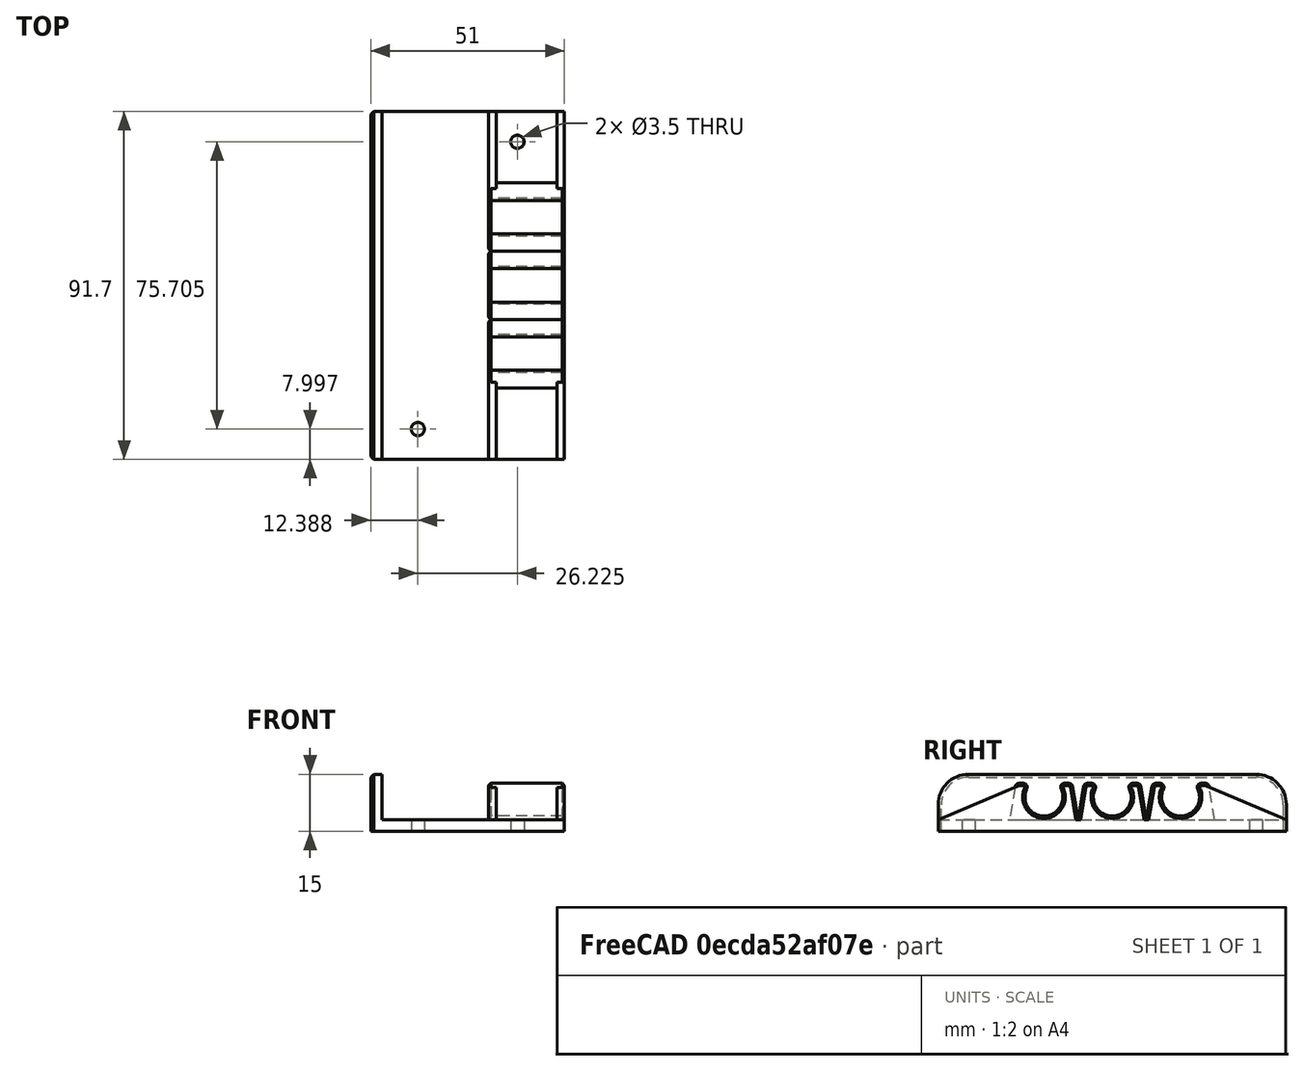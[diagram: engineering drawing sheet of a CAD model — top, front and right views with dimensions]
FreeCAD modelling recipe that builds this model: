
FCSTD DOCUMENT  (FreeCAD 0.21R33771 (Git))
Label: SDS-Plus_ClipHolder
License: All rights reserved
LicenseURL: https://en.wikipedia.org/wiki/All_rights_reserved
objects: Sketcher::SketchObject×7, PartDesign::Pad×6, PartDesign::Chamfer×4, PartDesign::LinearPattern×2, PartDesign::Body×2, PartDesign::SubShapeBinder×2, PartDesign::Fillet×1, PartDesign::FeatureBase×1, Mesh::Feature×1, Part::Feature×1, Spreadsheet::Sheet×1, PartDesign::Hole×1
note: 39 computed .brp shape members not serialized (recipe doc carries the construction recipe); baked Part::Feature solids carry a one-line shape summary decoded from their .brp

FEATURE [Sketcher::SketchObject] Sketch
  FullyConstrained = true
  MapMode = 5
  Placement = pos=(0,0,0) rot=(0.57735,0.57735,0.57735;2.0944rad)
  Support = -> [YZ_Plane]
  sketch-geometry (15):
    g0: ArcOfCircle CenterX=9 CenterY=6 CenterZ=0 NormalX=0 NormalY=0 NormalZ=1 AngleXU=0 Radius=5 StartAngle=2.69057 EndAngle=6.73421
    g1: LineSegment StartX=3.6 StartY=9.61534 StartZ=0 EndX=2.44735 EndY=9.61534 EndZ=0
    g2: LineSegment StartX=1.46091 StartY=8.77948 StartZ=0 EndX=0 EndY=0 EndZ=0
    g3: LineSegment StartX=0 StartY=0 StartZ=0 EndX=18 EndY=0 EndZ=0
    g4: LineSegment StartX=18 StartY=0 StartZ=0 EndX=16.5391 EndY=8.77948 EndZ=0
    g5: LineSegment StartX=15.5527 StartY=9.61534 StartZ=0 EndX=14.4 EndY=9.61534 EndZ=0
    g6: LineSegment StartX=9 StartY=6 StartZ=0 EndX=9 EndY=1 EndZ=0
    g7: LineSegment StartX=9 StartY=6 StartZ=0 EndX=4 EndY=6 EndZ=0
    g8: ArcOfCircle CenterX=3.6 CenterY=8.61534 CenterZ=0 NormalX=0 NormalY=0 NormalZ=1 AngleXU=0 Radius=1 StartAngle=5.83216 EndAngle=7.85398
    g9: ArcOfCircle CenterX=14.4 CenterY=8.61534 CenterZ=0 NormalX=0 NormalY=0 NormalZ=1 AngleXU=0 Radius=1 StartAngle=1.5708 EndAngle=3.59262
    g10: LineSegment StartX=4.5 StartY=8.17945 StartZ=0 EndX=13.5 EndY=8.17945 EndZ=0
    g11: ArcOfCircle CenterX=15.5527 CenterY=8.61534 CenterZ=0 NormalX=0 NormalY=0 NormalZ=1 AngleXU=0 Radius=1 StartAngle=0.16489 EndAngle=1.5708
    g12: GeomPoint X=16.4 Y=9.61534 Z=0
    g13: ArcOfCircle CenterX=2.44735 CenterY=8.61534 CenterZ=0 NormalX=0 NormalY=0 NormalZ=1 AngleXU=0 Radius=1 StartAngle=1.5708 EndAngle=2.9767
    g14: GeomPoint X=1.6 Y=9.61534 Z=0
  constraints (38):
    c: Diameter(g0) = 10
    c: Horizontal(g1)
    c: Coincident(g2,g-1)
    c: Coincident(g2,g3)
    c: PointOnObject(g3,g-1)
    c: Coincident(g3,g4)
    c: Horizontal(g5)
    c: Coincident(g6,g0)
    c: PointOnObject(g6,g0)
    c: Vertical(g6)
    c: Coincident(g7,g0)
    c: PointOnObject(g7,g0)
    c: Horizontal(g7)
    c: DistanceY(g2,g6) = 1
    c: DistanceX(g2,g7) = 4
    c: Tangent(g1,g8) = -1.5708
    c: Tangent(g0,g8) = 1.5708
    c: Tangent(g0,g9) = 1.5708
    c: Tangent(g5,g9) = -1.5708
    c: Equal(g8,g9)
    c: Coincident(g10,g0)
    c: Coincident(g10,g0)
    c: Horizontal(g10)
    c: DistanceX(g10,g10) = 9
    c: Radius(g8) = 1
    c: DistanceX(g3,g3) = 18
    c: DistanceX(g5,g12) = 2
    c: PointOnObject(g12,g5)
    c: PointOnObject(g12,g4)
    c: Tangent(g5,g11) = -1.5708
    c: Tangent(g4,g11) = -1.5708
    c: PointOnObject(g14,g1)
    c: PointOnObject(g14,g2)
    c: Tangent(g1,g13) = -1.5708
    c: Tangent(g2,g13) = -1.5708
    c: Equal(g11,g13)
    c: Radius(g13) = 1
    c: DistanceX(g14,g1) = 2
FEATURE [PartDesign::Pad] Pad
  Direction = (1,-2e-16,3e-16)
  Length = 20
  Length2 = 10
  Placement = pos=(0,0,0) rot=(1,1,1;2.0944rad)
  Profile = -> Sketch
  ReferenceAxis = -> Sketch [N_Axis]
  Type = 0
FEATURE [Sketcher::SketchObject] Sketch001
  FullyConstrained = true
  MapMode = 5
  Placement = pos=(0,0,0) rot=(1,0,0;1.5708rad)
  Support = -> [XZ_Plane]
  sketch-geometry (6):
    g0: LineSegment StartX=20 StartY=-3 StartZ=0 EndX=-31 EndY=-3 EndZ=0
    g1: LineSegment StartX=-28 StartY=0 StartZ=0 EndX=20 EndY=0 EndZ=0
    g2: LineSegment StartX=20 StartY=0 StartZ=0 EndX=20 EndY=-3 EndZ=0
    g3: LineSegment StartX=-31 StartY=-3 StartZ=0 EndX=-31 EndY=11 EndZ=0
    g4: LineSegment StartX=-31 StartY=11 StartZ=0 EndX=-28 EndY=11 EndZ=0
    g5: LineSegment StartX=-28 StartY=11 StartZ=0 EndX=-28 EndY=0 EndZ=0
  constraints (18):
    c: Coincident(g1,g2)
    c: Coincident(g2,g0)
    c: Horizontal(g0)
    c: Horizontal(g1)
    c: Vertical(g2)
    c: PointOnObject(g1,g-1)
    c: DistanceX(g-1,g1) = 20
    c: DistanceX(g1,g-1) = 28
    c: Coincident(g0,g3)
    c: Vertical(g3)
    c: Coincident(g3,g4)
    c: Horizontal(g4)
    c: Coincident(g4,g5)
    c: Coincident(g5,g1)
    c: Vertical(g5)
    c: DistanceX(g4,g4) = 3
    c: DistanceY(g2,g2) = 3
    c: DistanceY(g5,g5) = 11
FEATURE [PartDesign::Chamfer] Chamfer
  Angle = 45
  Base = -> Pad [Edge25,Edge28,Edge30,Edge4,Edge7,Edge10,Edge13,Edge16,Edge19,Edge18,Edge15,Edge12,Edge9,Edge6,Edge3,Edge29,Edge27,Edge24]
  BaseFeature = -> Pad
  ChamferType = 0
  FlipDirection = false
  Placement = pos=(0,0,0) rot=(1,1,1;2.0944rad)
  Size = 0.6
  Size2 = 1
  SupportTransform = false
  UseAllEdges = false
FEATURE [PartDesign::Pad] Pad001
  BaseFeature = -> Chamfer
  Direction = (0,-1,-2e-16)
  Length = 18
  Length2 = 10
  Placement = pos=(0,0,0) rot=(1,1,1;2.0944rad)
  Profile = -> Sketch001
  ReferenceAxis = -> Sketch001 [N_Axis]
  Reversed = true
  Type = 0
FEATURE [PartDesign::LinearPattern] LinearPattern
  BaseFeature = -> Pad001
  Direction = -> Sketch001 [N_Axis]
  Length = 36
  Occurrences = 3
  Originals = -> [Pad001,Pad,Chamfer]
  Placement = pos=(0,0,0) rot=(1,1,1;2.0944rad)
FEATURE [PartDesign::Fillet] Fillet
  Base = -> LinearPattern [Edge118,Edge148]
  BaseFeature = -> LinearPattern
  Placement = pos=(0,0,0) rot=(1,1,1;2.0944rad)
  Radius = 8
  SupportTransform = false
  UseAllEdges = false
FEATURE [PartDesign::Chamfer] Chamfer001
  Angle = 45
  Base = -> Fillet [Edge5,Edge118]
  BaseFeature = -> Fillet
  ChamferType = 0
  FlipDirection = false
  Placement = pos=(0,0,0) rot=(1,1,1;2.0944rad)
  Size = 0.6
  Size2 = 1
  SupportTransform = false
  UseAllEdges = false
FEATURE [PartDesign::Chamfer] Chamfer002
  Angle = 45
  Base = -> Chamfer001 [Edge3,Edge16,Edge15,Edge40,Edge85,Edge86,Edge94,Edge93,Edge49,Edge25,Edge22,Vertex6,Edge95,Edge7,Edge87,Edge124,Edge8]
  BaseFeature = -> Chamfer001
  ChamferType = 0
  FlipDirection = false
  Placement = pos=(0,0,0) rot=(1,1,1;2.0944rad)
  Size = 0.6
  Size2 = 1
  SupportTransform = false
  UseAllEdges = false
FEATURE [PartDesign::Body] Body  label="SDS Clip Body"
  Group = -> [Sketch,Pad,Sketch001,Chamfer,Pad001,LinearPattern,Fillet,Chamfer001,Chamfer002]
  Origin = -> Origin
  Tip = -> Chamfer002
FEATURE [PartDesign::FeatureBase] BaseFeature
  BaseFeature = -> Body
FEATURE [Mesh::Feature] L_Boxx_Lid_Mount_Body  label="L-Boxx_Lid_Mount-Body"
FEATURE [Part::Feature] L_Boxx_Lid_Mount_Body001
  shape: bbox 38.95 x 88.43 x 1 mm, 228 faces, 0 solids (baked)
FEATURE [PartDesign::SubShapeBinder] Binder  label="L-Boxx-lid-mount"
  BindCopyOnChange = 0
  BindMode = 0
  ClaimChildren = false
  Context = -> Body001 [Binder.]
  Fuse = false
  MakeFace = true
  OffsetFill = false
  OffsetIntersection = false
  OffsetJoinType = 0
  OffsetOpenResult = false
  PartialLoad = false
  Relative = true
  Support = -> [L_Boxx_Lid_Mount_Body001]
  _Version = 2
FEATURE [Sketcher::SketchObject] Sketch002  label="OriginalMountHoleSketch"
  ExternalGeometry = -> [Binder,BaseFeature]
  FullyConstrained = true
  MapMode = 5
  Support = -> [XY_Plane001]
  sketch-geometry (2):
    g0: Circle CenterX=26.2251 CenterY=45.4231 CenterZ=0 NormalX=0 NormalY=0 NormalZ=1 AngleXU=0 Radius=1.50002
    g1: Circle CenterX=0.000238433 CenterY=-30.282 CenterZ=0 NormalX=0 NormalY=0 NormalZ=1 AngleXU=0 Radius=1.50002
  constraints (10):
    c: PointOnObject(g-5,g0)
    c: PointOnObject(g-5,g0)
    c: PointOnObject(g-7,g0)
    c: PointOnObject(g-3,g1)
    c: PointOnObject(g-3,g1)
    c: PointOnObject(g-4,g1)
    c: DistanceY(g-9,g0) = 27.4231  'y1'
    c: DistanceY(g-8,g1) = 5.71795  'y2'
    c: DistanceX(g-9,g0) = 6.82513  'x1'
    c: DistanceX(g-8,g1) = 30.4002  'x2'
FEATURE [PartDesign::SubShapeBinder] Binder001
  BindCopyOnChange = 0
  BindMode = 0
  ClaimChildren = false
  Context = -> Body001 [Binder001.]
  Fuse = false
  MakeFace = true
  OffsetFill = false
  OffsetIntersection = false
  OffsetJoinType = 0
  OffsetOpenResult = false
  PartialLoad = false
  Placement = pos=(-18.6127,-16.5705,0) rot=(0,0,1;0rad)
  Relative = true
  Support = -> [Sketch002]
  _Version = 2
  expr: .Placement.Base.x = <<offset>>.x
  expr: .Placement.Base.y = <<offset>>.y
FEATURE [Spreadsheet::Sheet] Spreadsheet  label="offset"
  cells = A1='x; B1(x)==-(x2 + x1) / 2; A2='y; B2(y)==-(y1 + y2) / 2; A4='x1; B4(x1)==<<OriginalMountHoleSketch>>.Constraints.x1; A5='x2; B5(x2)==<<OriginalMountHoleSketch>>.Constraints.x2; A6='y1; B6(y1)==<<OriginalMountHoleSketch>>.Constraints.y1; A7='y2; B7(y2)==<<OriginalMountHoleSketch>>.Constraints.y2
FEATURE [Sketcher::SketchObject] Sketch003
  ExternalGeometry = -> [BaseFeature,Binder001]
  FullyConstrained = true
  MapMode = 5
  Support = -> [XY_Plane001]
  sketch-geometry (6):
    g0: LineSegment StartX=-31 StartY=-54.8526 StartZ=0 EndX=20 EndY=-54.8526 EndZ=0
    g1: LineSegment StartX=20 StartY=-54.8526 StartZ=0 EndX=20 EndY=36.8526 EndZ=0
    g2: LineSegment StartX=20 StartY=36.8526 StartZ=0 EndX=-31 EndY=36.8526 EndZ=0
    g3: LineSegment StartX=-31 StartY=36.8526 StartZ=0 EndX=-31 EndY=-54.8526 EndZ=0
    g4: LineSegment StartX=-18.6124 StartY=-46.8526 StartZ=0 EndX=-18.6124 EndY=-54.8526 EndZ=0
    g5: LineSegment StartX=7.61245 StartY=28.8526 StartZ=0 EndX=7.61245 EndY=36.8526 EndZ=0
  constraints (18):
    c: Coincident(g0,g1)
    c: Coincident(g1,g2)
    c: Coincident(g2,g3)
    c: Coincident(g3,g0)
    c: Horizontal(g0)
    c: Horizontal(g2)
    c: Vertical(g1)
    c: Vertical(g3)
    c: PointOnObject(g-3,g3)
    c: PointOnObject(g-4,g1)
    c: Coincident(g4,g-6)
    c: PointOnObject(g4,g0)
    c: Vertical(g4)
    c: Coincident(g5,g-5)
    c: PointOnObject(g5,g2)
    c: Vertical(g5)
    c: Equal(g5,g4)
    c: DistanceY(g4,g4) = 8
FEATURE [PartDesign::Pad] Pad002
  BaseFeature = -> BaseFeature
  Direction = (0,0,1)
  Length = 3
  Length2 = 10
  Profile = -> Sketch003
  ReferenceAxis = -> Sketch003 [N_Axis]
  Reversed = true
  Type = 0
FEATURE [Sketcher::SketchObject] Sketch004
  ExternalGeometry = -> [Pad002]
  FullyConstrained = true
  MapMode = 5
  Placement = pos=(0,0,0) rot=(0.57735,0.57735,0.57735;2.0944rad)
  Support = -> [YZ_Plane001]
  sketch-geometry (3):
    g0: LineSegment StartX=-54.8526 StartY=0 StartZ=0 EndX=-33.5527 EndY=0 EndZ=0
    g1: LineSegment StartX=-33.5527 StartY=0 StartZ=0 EndX=-33.5527 EndY=9.01534 EndZ=0
    g2: LineSegment StartX=-33.5527 StartY=9.01534 StartZ=0 EndX=-54.8526 EndY=0 EndZ=0
  constraints (7):
    c: Coincident(g-4,g0)
    c: Horizontal(g0)
    c: Coincident(g0,g1)
    c: Coincident(g1,g2)
    c: Coincident(g2,g0)
    c: Coincident(g1,g-3)
    c: Vertical(g1)
FEATURE [PartDesign::Pad] Pad003
  BaseFeature = -> Pad002
  Direction = (1,-2e-16,3e-16)
  Length = 2
  Length2 = 10
  Profile = -> Sketch004
  ReferenceAxis = -> Sketch004 [N_Axis]
  Type = 0
FEATURE [Sketcher::SketchObject] Sketch005
  ExternalGeometry = -> [Pad003]
  FullyConstrained = true
  MapMode = 5
  Placement = pos=(0,0,0) rot=(0.57735,0.57735,0.57735;2.0944rad)
  Support = -> [YZ_Plane001]
  sketch-geometry (3):
    g0: LineSegment StartX=15.5527 StartY=9.01534 StartZ=0 EndX=15.5527 EndY=0 EndZ=0
    g1: LineSegment StartX=15.5527 StartY=0 StartZ=0 EndX=36.8526 EndY=0 EndZ=0
    g2: LineSegment StartX=36.8526 StartY=0 StartZ=0 EndX=15.5527 EndY=9.01534 EndZ=0
  constraints (7):
    c: Coincident(g-4,g0)
    c: PointOnObject(g0,g-1)
    c: Vertical(g0)
    c: Coincident(g0,g1)
    c: Coincident(g1,g-3)
    c: Coincident(g1,g2)
    c: Coincident(g2,g0)
FEATURE [PartDesign::Pad] Pad004
  BaseFeature = -> Pad003
  Direction = (1,-2e-16,3e-16)
  Length = 2
  Length2 = 10
  Profile = -> Sketch005
  ReferenceAxis = -> Sketch005 [N_Axis]
  Type = 0
FEATURE [PartDesign::LinearPattern] LinearPattern001
  BaseFeature = -> Pad004
  Direction = -> Sketch005 [N_Axis]
  Length = 18
  Occurrences = 2
  Originals = -> [Pad004,Pad003]
FEATURE [Sketcher::SketchObject] Sketch006
  ExternalGeometry = -> [LinearPattern001]
  FullyConstrained = true
  MapMode = 5
  Placement = pos=(-31,3.4e-15,6.9e-15) rot=(0.57735,-0.57735,-0.57735;2.0944rad)
  Support = -> [LinearPattern001]
  sketch-geometry (7):
    g0: LineSegment StartX=-36.8526 StartY=-8.9e-15 StartZ=0 EndX=54.8526 EndY=-8.9e-15 EndZ=0
    g1: LineSegment StartX=54.8526 StartY=-8.9e-15 StartZ=0 EndX=54.8526 EndY=4 EndZ=0
    g2: LineSegment StartX=46.8526 StartY=12 StartZ=0 EndX=-28.8526 EndY=12 EndZ=0
    g3: LineSegment StartX=-36.8526 StartY=4 StartZ=0 EndX=-36.8526 EndY=-8.9e-15 EndZ=0
    g4: ArcOfCircle CenterX=46.8526 CenterY=4 CenterZ=0 NormalX=0 NormalY=0 NormalZ=1 AngleXU=0 Radius=8 StartAngle=1.257e-13 EndAngle=1.5708
    g5: ArcOfCircle CenterX=-28.8526 CenterY=4 CenterZ=0 NormalX=0 NormalY=0 NormalZ=1 AngleXU=0 Radius=8 StartAngle=1.5708 EndAngle=3.14159
    g6: LineSegment StartX=18 StartY=11 StartZ=0 EndX=18 EndY=12 EndZ=0
  constraints (18):
    c: Coincident(g0,g1)
    c: Coincident(g3,g0)
    c: Horizontal(g0)
    c: Horizontal(g2)
    c: Vertical(g1)
    c: Vertical(g3)
    c: Coincident(g0,g-4)
    c: PointOnObject(g0,g-3)
    c: Tangent(g1,g4) = -1.5708
    c: Tangent(g2,g4) = -1.5708
    c: Tangent(g2,g5) = -1.5708
    c: Tangent(g3,g5) = -1.5708
    c: Equal(g5,g4)
    c: Radius(g5) = 8
    c: Coincident(g6,g-5)
    c: PointOnObject(g6,g2)
    c: Vertical(g6)
    c: DistanceY(g6,g6) = 1
FEATURE [PartDesign::Pad] Pad005
  BaseFeature = -> LinearPattern001
  Direction = (-1,2e-16,2e-16)
  Length = 10
  Length2 = 10
  Profile = -> Sketch006
  ReferenceAxis = -> Sketch006 [N_Axis]
  Reversed = true
  Type = 3
  UpToFace = -> LinearPattern001 [Face64]
FEATURE [PartDesign::Chamfer] Chamfer003
  Angle = 45
  Base = -> Pad005 [Edge43,Edge77,Edge78,Edge79,Edge80,Edge126,Edge17]
  BaseFeature = -> Pad005
  ChamferType = 0
  FlipDirection = false
  Size = 0.8
  Size2 = 1
  SupportTransform = false
  UseAllEdges = false
FEATURE [PartDesign::Hole] Hole
  BaseFeature = -> Chamfer003
  CustomThreadClearance = 0
  Depth = 214.118
  DepthType = 1
  Diameter = 3.5
  DrillForDepth = false
  DrillPoint = 1
  DrillPointAngle = 118
  HoleCutCountersinkAngle = 90
  HoleCutCustomValues = false
  HoleCutDepth = 0
  HoleCutDiameter = 6.1
  HoleCutType = 0
  ModelThread = false
  Profile = -> Binder001
  Tapered = false
  TaperedAngle = 90
  ThreadClass = 0
  ThreadDepth = 214.118
  ThreadDepthType = 0
  ThreadDirection = 0
  ThreadFit = 0
  ThreadSize = 0
  ThreadType = 0
  Threaded = false
  UseCustomThreadClearance = false
FEATURE [PartDesign::Body] Body001  label="L-Boxx Mount Body"
  BaseFeature = -> Body
  Group = -> [BaseFeature,Binder,Sketch002,Binder001,Sketch003,Pad002,Sketch004,Pad003,Sketch005,Pad004,LinearPattern001,Sketch006,Pad005,Chamfer003,Hole]
  Origin = -> Origin001
  Tip = -> Hole
